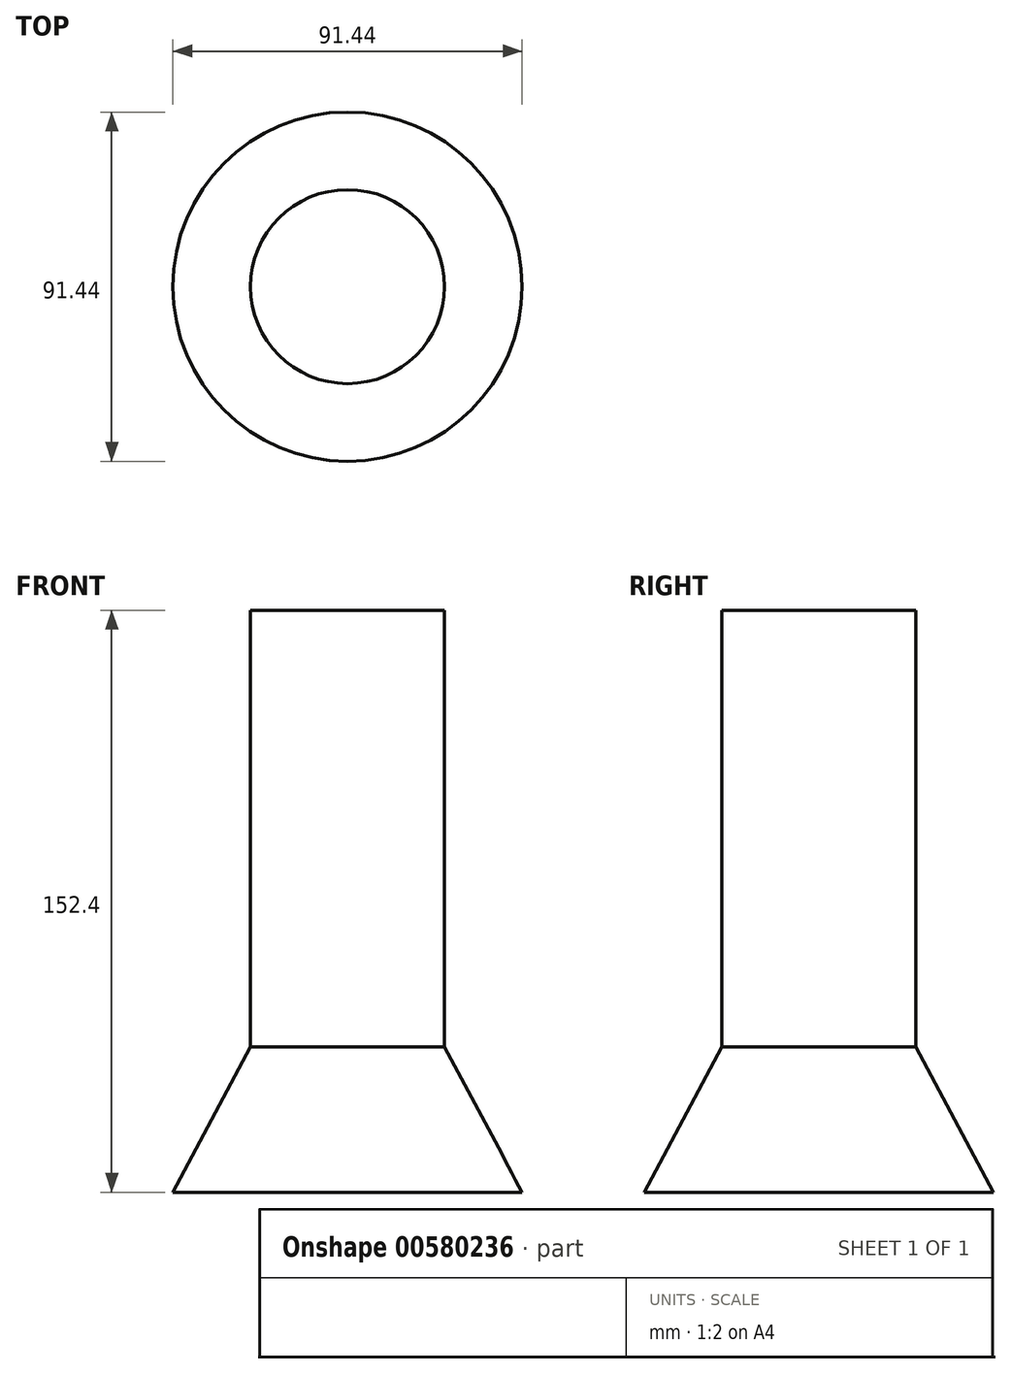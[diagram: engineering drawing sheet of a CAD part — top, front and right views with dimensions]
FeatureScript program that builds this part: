
annotation { "Feature Type Name" : "Feature", "Feature Type Description" : "" }
export const myFeature = defineFeature(function(context is Context, id is Id, definition is map)
    precondition{}
    {
        {
            var Q0;
            Q0=qCreatedBy(makeId("Front.planeOp"),FACE);
            var sketch = newSketch(context, id + "F0", { "sketchPlane" : qUnion([Q0])});
            skLineSegment(sketch, "E0", {"start": v(0, 0) * mm, "end": v(45.72, 0) * mm});
            skLineSegment(sketch, "E1", {"start": v(45.72, 0) * mm, "end": v(25.4, 38.1) * mm});
            skLineSegment(sketch, "E2", {"start": v(25.4, 38.1) * mm, "end": v(0, 38.1) * mm});
            skLineSegment(sketch, "E3", {"start": v(0, 38.1) * mm, "end": v(0, 0) * mm});
            skSolve(sketch);
        }
        {
            var Q0;
            Q0=makeQuery(id+"F0.imprint","IMPRINT",FACE,{"disambiguationData":[TD([[makeQuery(id+"F0.imprint","IMPRINT",EDGE,{"derivedFrom":sQuery(id+"F0.wireOp",EDGE,"E0")}),1.0]])]});
            var Q1;
            Q1=sQuery(id+"F0.wireOp",EDGE,"E3");
            revolve(context, id + "F1", {"entities" : qUnion([Q0]), "axis" : qUnion([Q1]), "revolveType" : RevolveType.FULL});
        }
        {
            var Q0;
            Q0=makeQuery(id+"F1.opRevolve","SWEPT_FACE",FACE,{"disambiguationData":[OSD([sQuery(id+"F0.wireOp",EDGE,"E2")])]});
            extrude(context, id + "F2", {"entities" : qUnion([Q0]), "depth" : 114.3 * mm, "offsetDistance" : 25.4 * mm});
        }
    });
